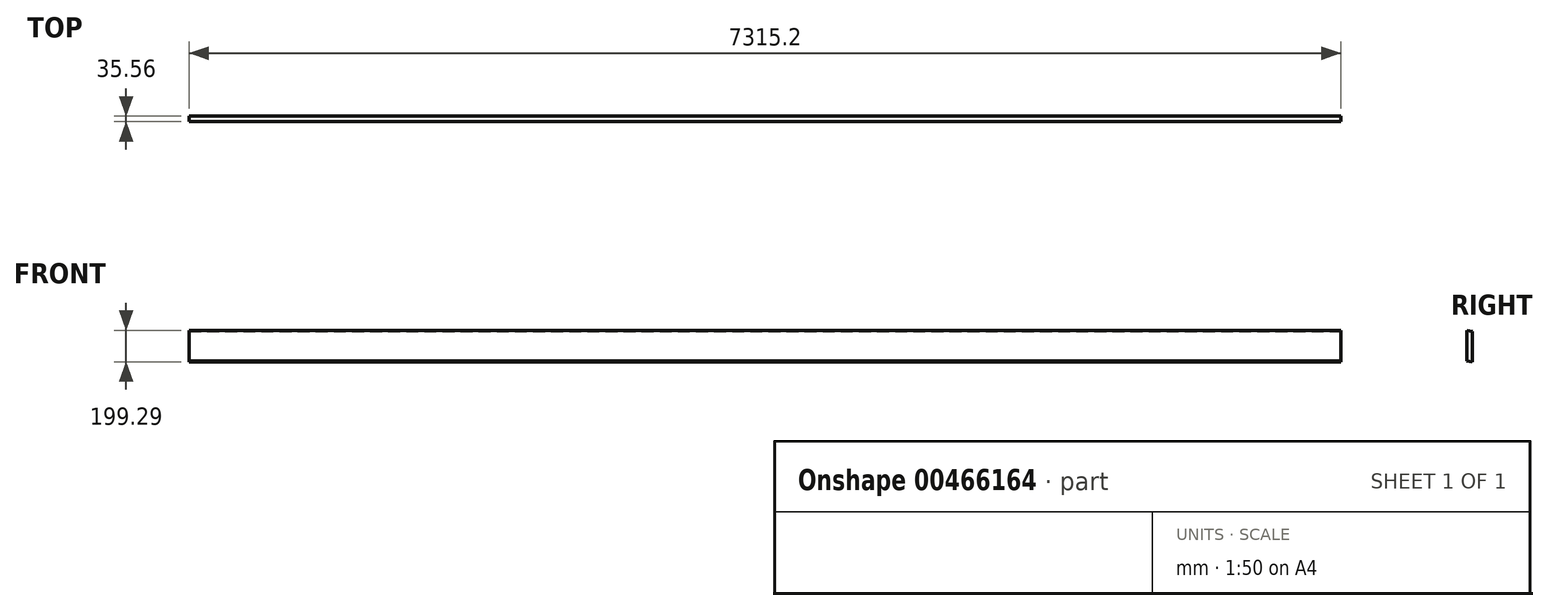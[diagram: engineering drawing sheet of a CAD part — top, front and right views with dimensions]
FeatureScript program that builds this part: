
annotation { "Feature Type Name" : "Feature", "Feature Type Description" : "" }
export const myFeature = defineFeature(function(context is Context, id is Id, definition is map)
    precondition{}
    {
        {
            var Q0;
            Q0=qCreatedBy(makeId("Right.planeOp"),FACE);
            var sketch = newSketch(context, id + "F0", { "sketchPlane" : qUnion([Q0])});
            skLineSegment(sketch, "E0", {"start": v(32.57, 188.3) * mm, "end": v(32.57, 0) * mm});
            skLineSegment(sketch, "E1", {"start": v(-3, 1.12) * mm, "end": v(24.55, -3.57) * mm});
            skLineSegment(sketch, "E2", {"start": v(24.55, -3.57) * mm, "end": v(32.57, -4.93) * mm});
            skLineSegment(sketch, "E3", {"start": v(32.57, 0) * mm, "end": v(32.57, -4.93) * mm});
            skLineSegment(sketch, "E4", {"start": v(-3, 1.12) * mm, "end": v(-3, 194.36) * mm});
            skLineSegment(sketch, "E5", {"start": v(9.13, 192.3) * mm, "end": v(-3, 194.36) * mm});
            skLineSegment(sketch, "E6", {"start": v(9.13, 192.3) * mm, "end": v(32.57, 188.3) * mm});
            skSolve(sketch);
        }
        {
            var Q0;
            Q0 = qSketchRegion(id + "F0", true);
            extrude(context, id + "F1", {"entities" : qUnion([Q0]), "oppositeDirection" : true, "depth" : 7315.2 * mm});
        }
    });
